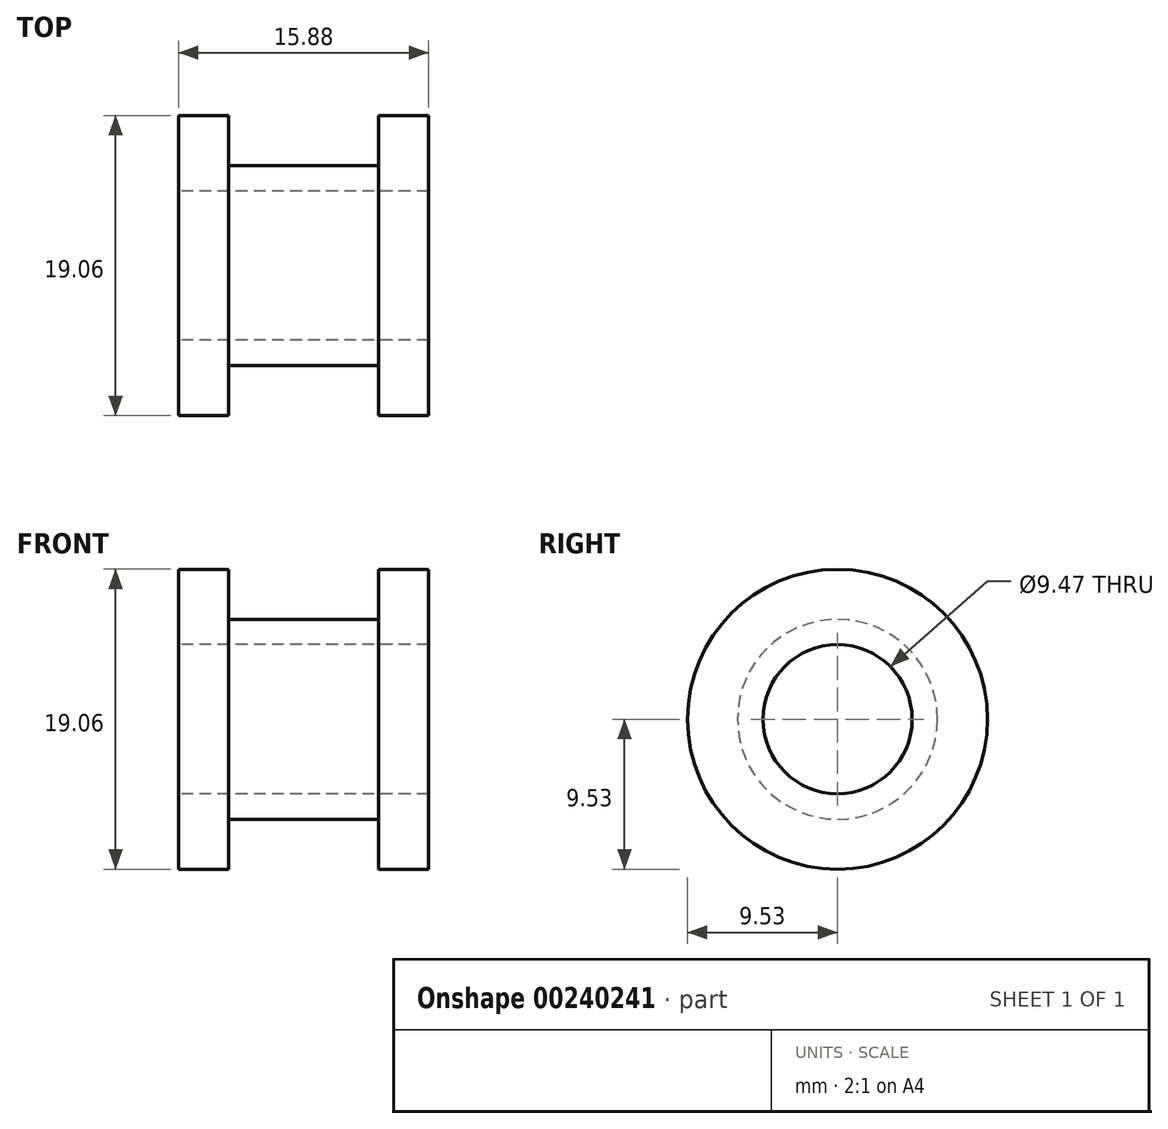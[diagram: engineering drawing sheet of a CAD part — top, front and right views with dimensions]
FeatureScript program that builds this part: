
annotation { "Feature Type Name" : "Feature", "Feature Type Description" : "" }
export const myFeature = defineFeature(function(context is Context, id is Id, definition is map)
    precondition{}
    {
        {
            var Q0;
            Q0=qCreatedBy(makeId("Front.planeOp"),FACE);
            var sketch = newSketch(context, id + "F0", { "sketchPlane" : qUnion([Q0])});
            skLineSegment(sketch, "E0", {"start": v(0, 4.74) * mm, "end": v(0, 6.35) * mm});
            skLineSegment(sketch, "E1", {"start": v(0, 6.35) * mm, "end": v(9.53, 6.35) * mm});
            skLineSegment(sketch, "E2", {"start": v(9.53, 6.35) * mm, "end": v(9.53, 9.53) * mm});
            skLineSegment(sketch, "E3", {"start": v(9.53, 9.53) * mm, "end": v(12.7, 9.53) * mm});
            skLineSegment(sketch, "E4", {"start": v(12.7, 9.53) * mm, "end": v(12.7, 4.74) * mm});
            skLineSegment(sketch, "E5", {"start": v(0, 4.74) * mm, "end": v(12.7, 4.74) * mm});
            skLineSegment(sketch, "E6", {"start": v(-9.31, 0) * mm, "end": v(28.97, 0) * mm, "construction": true});
            skLineSegment(sketch, "E7", {"start": v(0, 9.83) * mm, "end": v(9.53, 9.83) * mm, "construction": true});
            skLineSegment(sketch, "E8.bottom", {"start": v(0, 6.35) * mm, "end": v(0, 6.35) * mm});
            skLineSegment(sketch, "E8.top", {"start": v(0, 9.53) * mm, "end": v(0, 9.53) * mm});
            skLineSegment(sketch, "E8.left", {"start": v(0, 6.35) * mm, "end": v(0, 9.53) * mm});
            skLineSegment(sketch, "E8.right", {"start": v(0, 6.35) * mm, "end": v(0, 9.53) * mm});
            skLineSegment(sketch, "E9.bottom", {"start": v(0, 9.53) * mm, "end": v(-3.18, 9.53) * mm});
            skLineSegment(sketch, "E9.top", {"start": v(0, 9.53) * mm, "end": v(-3.18, 9.53) * mm});
            skLineSegment(sketch, "E9.right", {"start": v(-3.18, 9.53) * mm, "end": v(-3.18, 9.53) * mm});
            skLineSegment(sketch, "E10.top", {"start": v(-3.17, 4.74) * mm, "end": v(-3.17, 4.74) * mm});
            skLineSegment(sketch, "E10.left", {"start": v(-3.17, 9.53) * mm, "end": v(-3.17, 4.74) * mm});
            skLineSegment(sketch, "E10.right", {"start": v(-3.17, 9.53) * mm, "end": v(-3.17, 4.74) * mm});
            skLineSegment(sketch, "E11", {"start": v(-3.17, 4.74) * mm, "end": v(0, 4.74) * mm});
            skSolve(sketch);
        }
        {
            var Q0;
            Q0=makeQuery(id+"F0.imprint","IMPRINT",FACE,{"disambiguationData":[TD([[makeQuery(id+"F0.imprint","IMPRINT",EDGE,{"derivedFrom":sQuery(id+"F0.wireOp",EDGE,"E0")}),-1.0]])]});
            var Q1;
            Q1=makeQuery(id+"F0.imprint","IMPRINT",FACE,{"disambiguationData":[TD([[makeQuery(id+"F0.imprint","IMPRINT",EDGE,{"derivedFrom":sQuery(id+"F0.wireOp",EDGE,"E0")}),1.0]])]});
            var Q2;
            Q2=sQuery(id+"F0.wireOp",EDGE,"E6");
            var Q3;
            Q3=sQuery(id+"F0.wireOp",EDGE,"E4");
            var Q4;
            Q4=sQuery(id+"F0.wireOp",EDGE,"E0");
            var Q5;
            Q5=sQuery(id+"F0.wireOp",EDGE,"E5");
            var Q6;
            Q6=sQuery(id+"F0.wireOp",EDGE,"E1");
            var Q7;
            Q7=sQuery(id+"F0.wireOp",EDGE,"E2");
            var Q8;
            Q8=sQuery(id+"F0.wireOp",EDGE,"E3");
            var Q9;
            Q9=sQuery(id+"F0.wireOp",EDGE,"E6");
            revolve(context, id + "F1", {"entities" : qUnion([Q0, Q1]), "surfaceEntities" : qUnion([Q2, Q3, Q4, Q5, Q6, Q7, Q8]), "axis" : qUnion([Q9]), "revolveType" : RevolveType.FULL});
        }
    });
